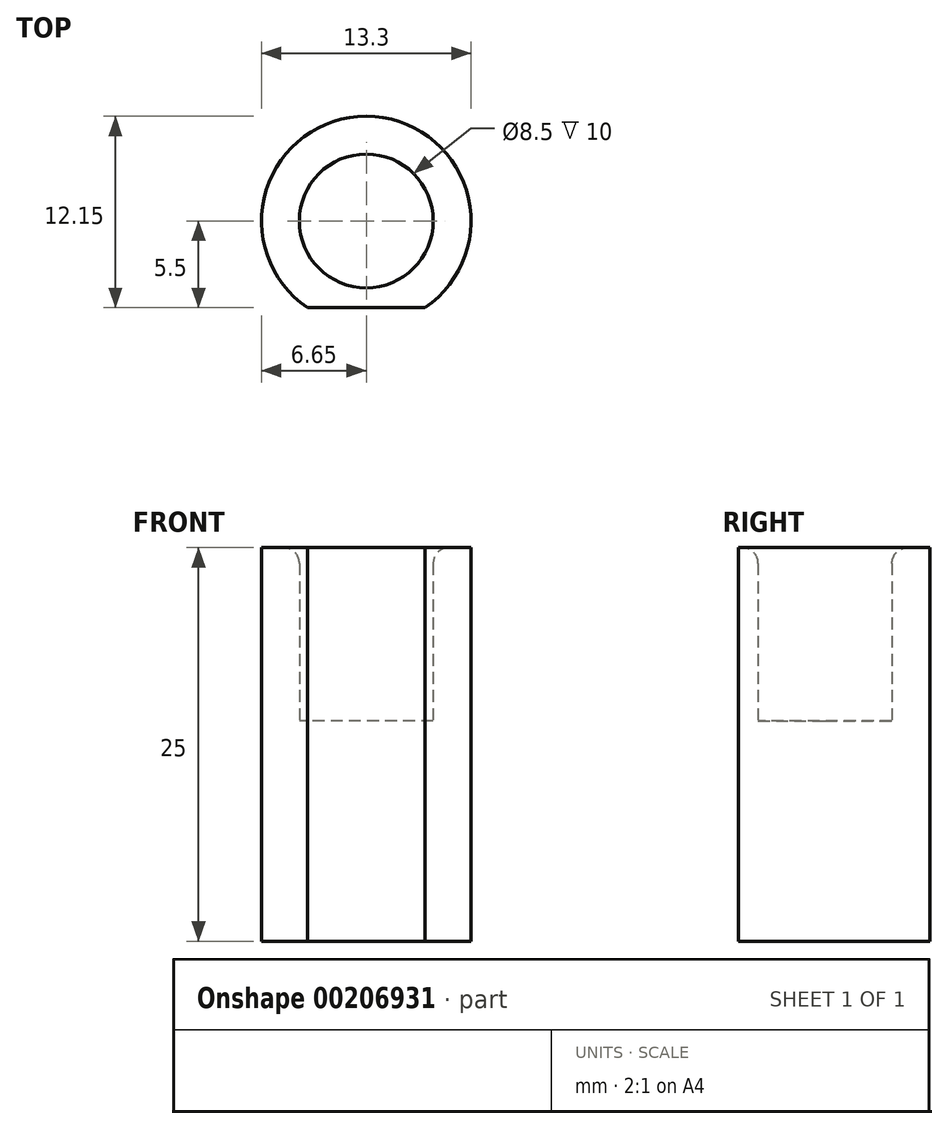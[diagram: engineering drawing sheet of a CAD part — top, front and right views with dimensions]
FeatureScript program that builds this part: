
annotation { "Feature Type Name" : "Feature", "Feature Type Description" : "" }
export const myFeature = defineFeature(function(context is Context, id is Id, definition is map)
    precondition{}
    {
        {
            var Q0;
            Q0=qCreatedBy(makeId("Top.planeOp"),FACE);
            var sketch = newSketch(context, id + "F0", { "sketchPlane" : qUnion([Q0])});
            skCircle(sketch, "E0", {"center": v(0, 0) * mm, "radius": 4.25 * mm});
            skArc(sketch, "E1", {"start": v(3.74, -5.5) * mm, "mid": v(0, 6.65) * mm, "end": v(-3.74, -5.5) * mm});
            skLineSegment(sketch, "E2", {"start": v(-3.74, -5.5) * mm, "end": v(3.74, -5.5) * mm});
            skSolve(sketch);
        }
        {
            var Q0;
            Q0=makeQuery(id+"F0.imprint","IMPRINT",FACE,{"disambiguationData":[TD([[makeQuery(id+"F0.imprint","IMPRINT",EDGE,{"derivedFrom":sQuery(id+"F0.wireOp",EDGE,"E0")}),1.0]])]});
            extrude(context, id + "F1", {"entities" : qUnion([Q0]), "depth" : 14 * mm});
        }
        {
            var Q0;
            Q0=makeQuery(id+"F0.imprint","IMPRINT",FACE,{"disambiguationData":[TD([[makeQuery(id+"F0.imprint","IMPRINT",EDGE,{"derivedFrom":sQuery(id+"F0.wireOp",EDGE,"E0")}),-1.0]])]});
            extrude(context, id + "F2", {"entities" : qUnion([Q0]), "operationType" : NewBodyOperationType.ADD, "depth" : 25 * mm});
        }
        {
            var Q0;
            Q0=makeQuery(id+"F1.opExtrude","CAP_EDGE",EDGE,{"disambiguationData":[OSD([sQuery(id+"F0.wireOp",EDGE,"E0")])],"isStart":false});
            var Q1;
            Q1=makeQuery(id+"F2.opExtrude","CAP_EDGE",EDGE,{"disambiguationData":[OSD([sQuery(id+"F0.wireOp",EDGE,"E0")])],"isStart":false});
            fillet(context, id + "F3", {"entities" : qUnion([Q0, Q1]), "radius" : 1 * mm, "tangentPropagation" : true, "allowEdgeOverflow" : false});
        }
    });
